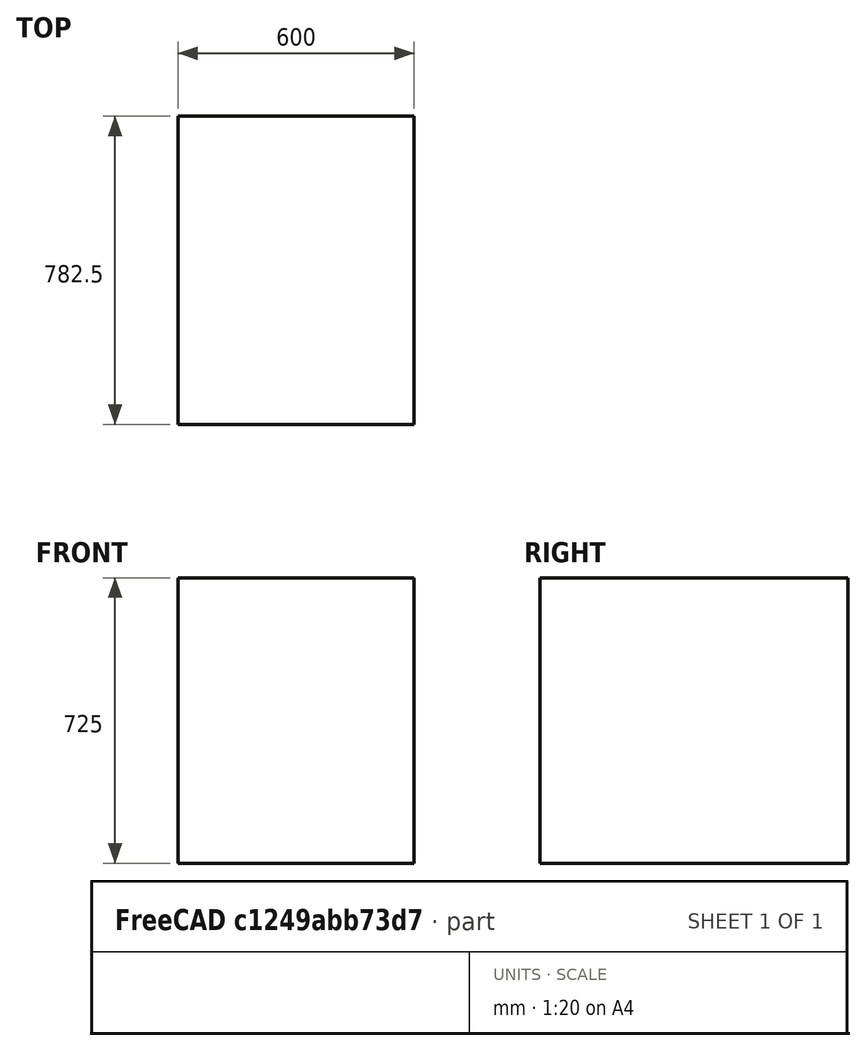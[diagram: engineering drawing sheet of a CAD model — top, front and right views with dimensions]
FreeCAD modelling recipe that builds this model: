
FCSTD DOCUMENT  (FreeCAD 0.19R24291 (Git))
Label: leftBuiltIn3-OneQuarter
License: All rights reserved
LicenseURL: http://en.wikipedia.org/wiki/All_rights_reserved
objects: Sketcher::SketchObject×1, PartDesign::Pad×1, PartDesign::Body×1
note: 4 computed .brp shape members not serialized (recipe doc carries the construction recipe); baked Part::Feature solids carry a one-line shape summary decoded from their .brp

FEATURE [Sketcher::SketchObject] Sketch
  FullyConstrained = false
  MapMode = 5
  Placement = pos=(0,0,0) rot=(0.57735,0.57735,0.57735;2.0944rad)
  Support = -> [YZ_Plane]
  expr: Constraints[29] = 8 * 12 * 25.4
  expr: Constraints[8] = 3130 / 4
  sketch-geometry (12):
    g0: LineSegment StartX=-782.5 StartY=725 StartZ=0 EndX=0 EndY=725 EndZ=0
    g1: LineSegment StartX=0 StartY=725 StartZ=0 EndX=0 EndY=0 EndZ=0
    g2: LineSegment StartX=0 StartY=0 StartZ=0 EndX=-782.5 EndY=0 EndZ=0
    g3: LineSegment StartX=-782.5 StartY=0 StartZ=0 EndX=-782.5 EndY=725 EndZ=0
    g4: LineSegment StartX=-3667.4 StartY=1853.05 StartZ=0 EndX=-537.403 EndY=1853.05 EndZ=0
    g5: LineSegment StartX=-537.403 StartY=1853.05 StartZ=0 EndX=-537.403 EndY=1128.05 EndZ=0
    g6: LineSegment StartX=-537.403 StartY=1128.05 StartZ=0 EndX=-3667.4 EndY=1128.05 EndZ=0
    g7: LineSegment StartX=-3667.4 StartY=1128.05 StartZ=0 EndX=-3667.4 EndY=1853.05 EndZ=0
    g8: LineSegment StartX=-3581.05 StartY=2612.82 StartZ=0 EndX=-1142.65 EndY=2612.82 EndZ=0
    g9: LineSegment StartX=-1142.65 StartY=2612.82 StartZ=0 EndX=-1142.65 EndY=2361.64 EndZ=0
    g10: LineSegment StartX=-1142.65 StartY=2361.64 StartZ=0 EndX=-3581.05 EndY=2361.64 EndZ=0
    g11: LineSegment StartX=-3581.05 StartY=2361.64 StartZ=0 EndX=-3581.05 EndY=2612.82 EndZ=0
  constraints (30):
    c: Coincident(g0,g1)
    c: Coincident(g1,g2)
    c: Coincident(g2,g3)
    c: Coincident(g3,g0)
    c: Horizontal(g0)
    c: Horizontal(g2)
    c: Vertical(g1)
    c: Vertical(g3)
    c: DistanceX(g2,g2) = 782.5
    c: DistanceY(g3,g3) = 725
    c: Coincident(g4,g5)
    c: Coincident(g5,g6)
    c: Coincident(g6,g7)
    c: Coincident(g7,g4)
    c: Horizontal(g4)
    c: Horizontal(g6)
    c: Vertical(g5)
    c: Vertical(g7)
    c: DistanceY(g7,g7) = 725
    c: DistanceX(g6,g6) = 3130
    c: Coincident(g1,g-1)
    c: Coincident(g8,g9)
    c: Coincident(g9,g10)
    c: Coincident(g10,g11)
    c: Coincident(g11,g8)
    c: Horizontal(g8)
    c: Horizontal(g10)
    c: Vertical(g9)
    c: Vertical(g11)
    c: DistanceX(g10,g10) = 2438.4
FEATURE [PartDesign::Pad] Pad
  Direction = (1,1,1)
  Length = 600
  Length2 = 100
  Placement = pos=(0,0,0) rot=(0.57735,0.57735,0.57735;2.0944rad)
  Profile = -> Sketch
  Type = 0
FEATURE [PartDesign::Body] Body
  Group = -> [Sketch,Pad]
  Origin = -> Origin
  Tip = -> Pad
